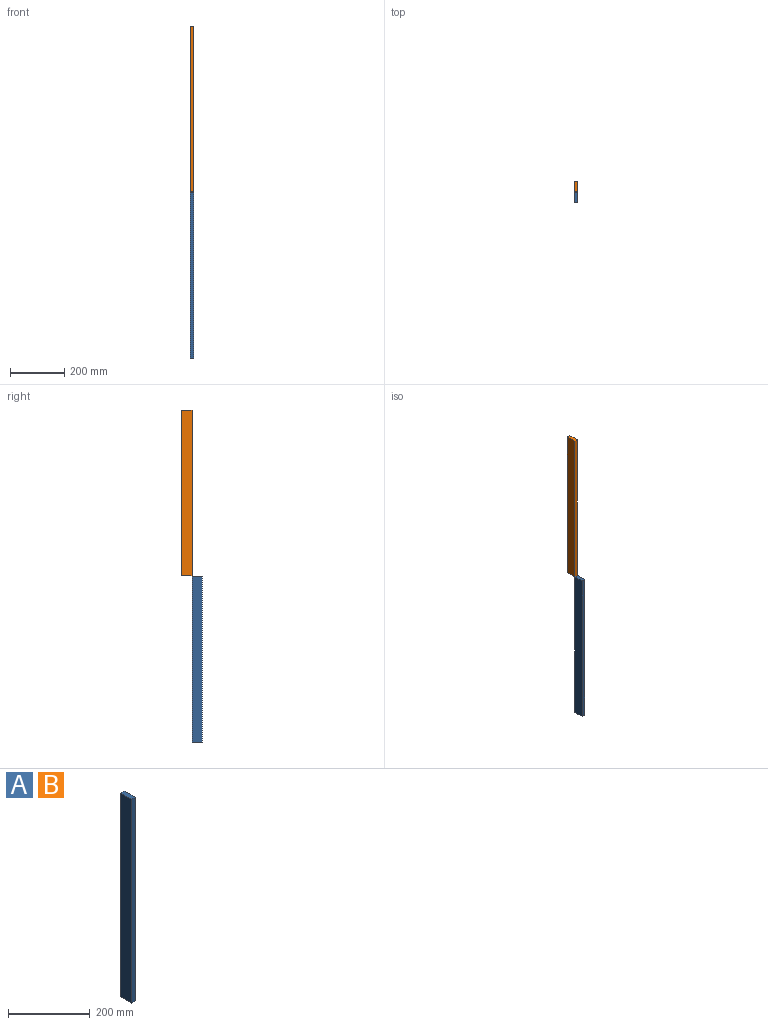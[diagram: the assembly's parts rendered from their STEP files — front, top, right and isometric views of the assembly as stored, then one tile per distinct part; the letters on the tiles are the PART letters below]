
ASSEMBLY  parts=2 mates=1
PART A: 6 faces, bbox 12.7x38.1x609.6 mm
  f0: plane 609.6x38.1mm, normal (-1,0,0), area 23225.8mm2, adj f1,f3,f4,f5
  f1: plane 609.6x12.7mm, normal (0,-1,0), area 7741.9mm2, adj f0,f2,f4,f5
  f2: plane 609.6x38.1mm, normal (1,0,0), area 23225.8mm2, adj f1,f3,f4,f5
  f3: plane 609.6x12.7mm, normal (0,1,0), area 7741.9mm2, adj f0,f2,f4,f5
  f4: plane 38.1x12.7mm, normal (0,0,1), area 483.9mm2, adj f0,f1,f2,f3
  f5: plane 38.1x12.7mm, normal (0,0,-1), area 483.9mm2, adj f0,f1,f2,f3
PART B: same geometry as A
PLACE A t=(180.67,60.48,-1227.8)mm
PLACE B t=(180.67,98.58,-618.2)mm
MATE fastened A.f4 <-> B.f5  axis (0,0,-1) through (193.37,98.58,-618.2)mm
